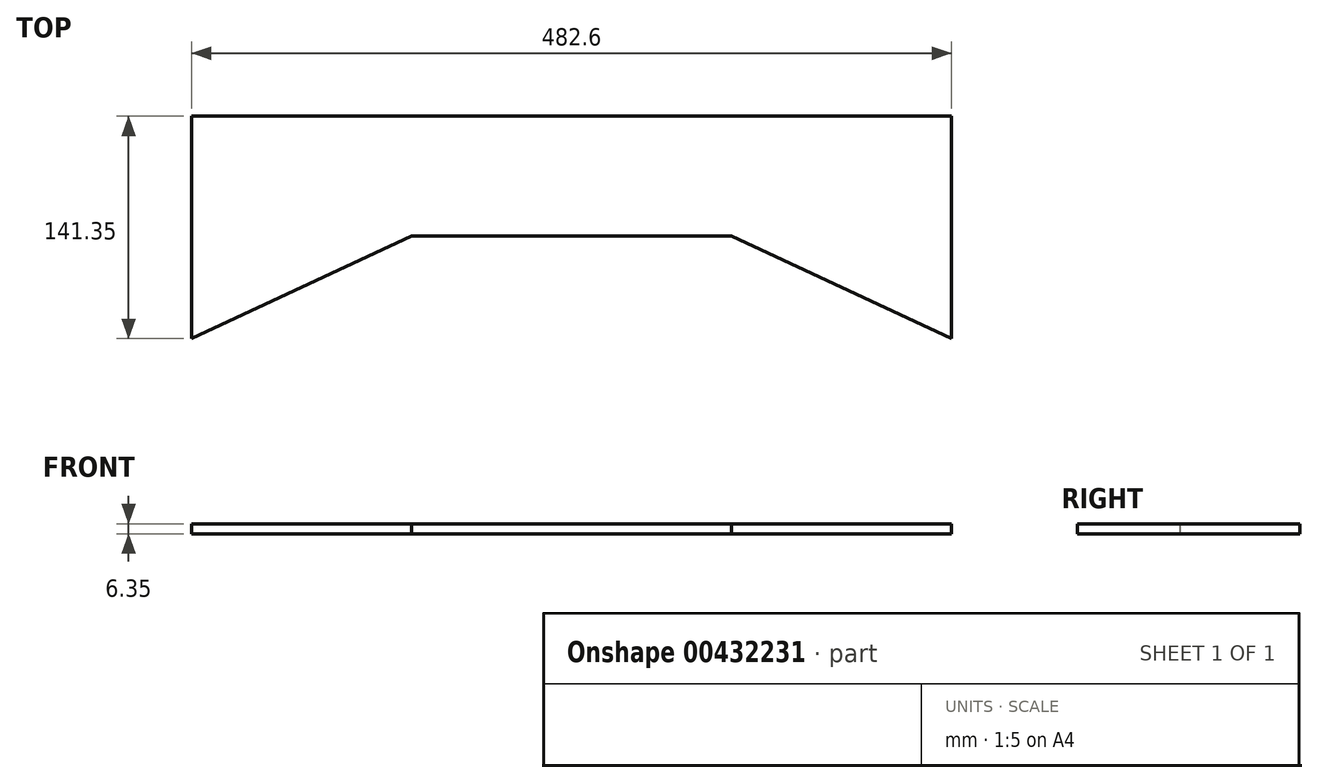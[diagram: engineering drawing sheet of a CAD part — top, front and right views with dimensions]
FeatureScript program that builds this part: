
annotation { "Feature Type Name" : "Feature", "Feature Type Description" : "" }
export const myFeature = defineFeature(function(context is Context, id is Id, definition is map)
    precondition{}
    {
        {
            var Q0;
            Q0=qCreatedBy(makeId("Top.planeOp"),FACE);
            var sketch = newSketch(context, id + "F0", { "sketchPlane" : qUnion([Q0])});
            skLineSegment(sketch, "E0", {"start": v(0, 0) * mm, "end": v(482.6, 0) * mm});
            skLineSegment(sketch, "E1", {"start": v(0, 0) * mm, "end": v(139.7, 0) * mm});
            skLineSegment(sketch, "E2", {"start": v(482.6, 0) * mm, "end": v(342.9, 0) * mm});
            skLineSegment(sketch, "E3", {"start": v(139.7, -76.2) * mm, "end": v(342.9, -76.2) * mm});
            skLineSegment(sketch, "E4", {"start": v(139.7, -76.2) * mm, "end": v(0, -141.34) * mm});
            skLineSegment(sketch, "E5", {"start": v(0, 0) * mm, "end": v(0, -141.34) * mm});
            skLineSegment(sketch, "E6", {"start": v(482.6, 0) * mm, "end": v(482.6, -141.35) * mm});
            skLineSegment(sketch, "E7", {"start": v(342.9, -76.2) * mm, "end": v(482.6, -141.35) * mm});
            skSolve(sketch);
        }
        {
            var Q0;
            Q0 = qSketchRegion(id + "F0", true);
            extrude(context, id + "F1", {"entities" : qUnion([Q0]), "depth" : 6.35 * mm});
        }
    });
